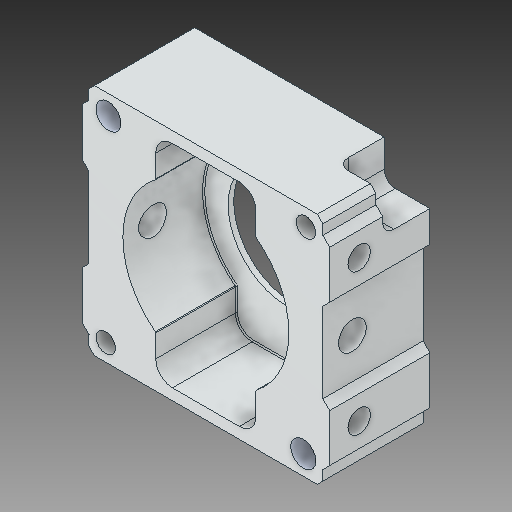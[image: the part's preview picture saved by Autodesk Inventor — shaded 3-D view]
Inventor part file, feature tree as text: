
AUTODESK INVENTOR PART (.ipt)
format: ipt  version: 2017 (Build 210142000, 142)  size: 271,872 bytes
history: native  units: in
note: dims shown in document units (in); Inventor stores cm internally (conversion verified against a paired STEP export)
features: chamfer x1
ambient origin geometry x8: Origin, YZ Plane, XZ Plane, XY Plane, X Axis, Y Axis, Z Axis, Center Point
bodies: Solid1 (feature_tree)
feature tree (1):
  chamfer  "Chamfer4"  [1 undecoded]
note: 1 required parameter value undecoded (feature->parameter linkage not recoverable at this tier; creation-order binding heuristic only, values carry confidence <= 0.55)
